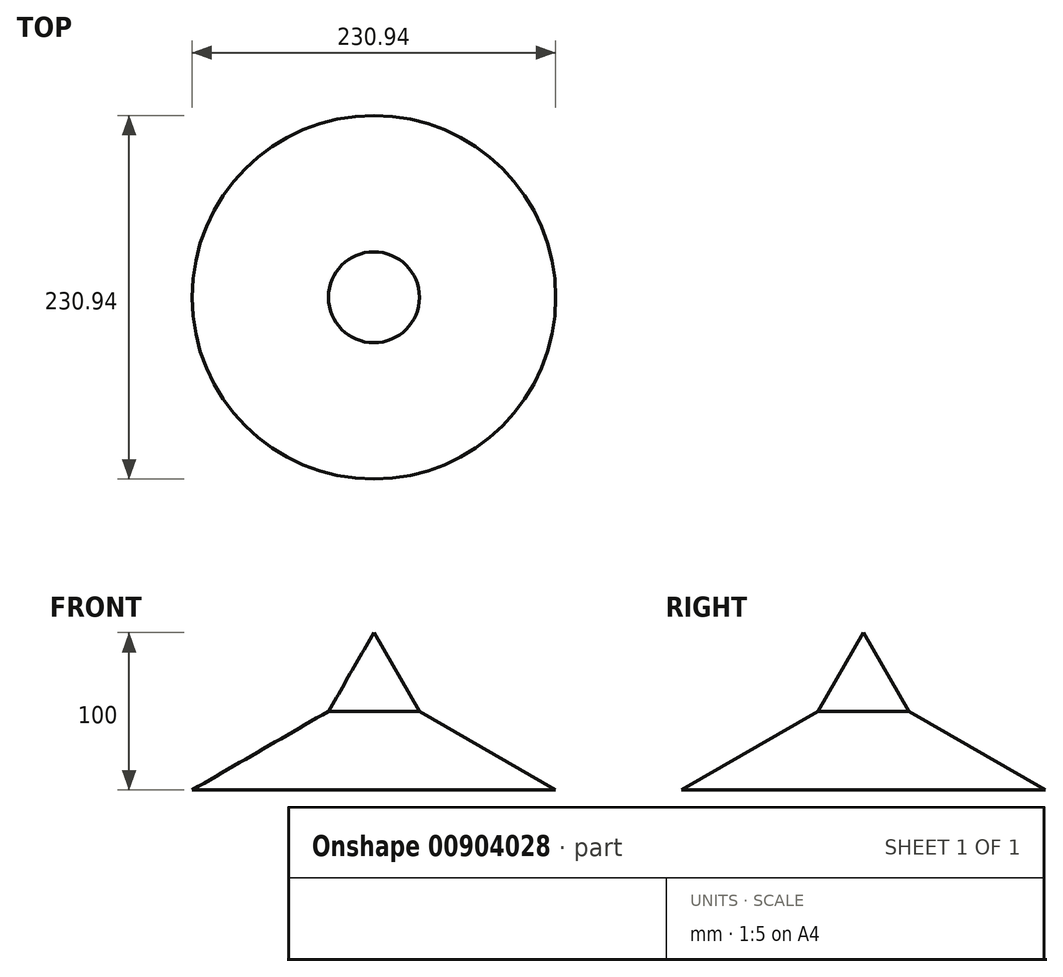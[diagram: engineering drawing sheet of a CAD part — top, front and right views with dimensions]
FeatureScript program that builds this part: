
annotation { "Feature Type Name" : "Feature", "Feature Type Description" : "" }
export const myFeature = defineFeature(function(context is Context, id is Id, definition is map)
    precondition{}
    {
        {
            var Q0;
            Q0=qCreatedBy(makeId("Front.planeOp"),FACE);
            var sketch = newSketch(context, id + "F0", { "sketchPlane" : qUnion([Q0])});
            skLineSegment(sketch, "E0", {"start": v(0, 0) * mm, "end": v(0, 100) * mm});
            skLineSegment(sketch, "E1", {"start": v(0, 100) * mm, "end": v(28.87, 50) * mm});
            skLineSegment(sketch, "E2", {"start": v(28.87, 50) * mm, "end": v(115.47, 0) * mm});
            skLineSegment(sketch, "E3", {"start": v(115.47, 0) * mm, "end": v(0, 0) * mm});
            skSolve(sketch);
        }
        {
            var Q0;
            Q0=makeQuery(id+"F0.imprint","IMPRINT",FACE,{"disambiguationData":[TD([[makeQuery(id+"F0.imprint","IMPRINT",EDGE,{"derivedFrom":sQuery(id+"F0.wireOp",EDGE,"E0")}),-1.0]])]});
            var Q1;
            Q1=sQuery(id+"F0.wireOp",EDGE,"E0");
            revolve(context, id + "F1", {"surfaceOperationType" : NewSurfaceOperationType.NEW, "entities" : qUnion([Q0]), "axis" : qUnion([Q1]), "revolveType" : RevolveType.FULL});
        }
        {
            var Q0;
            Q0=qCreatedBy(makeId("Right.planeOp"),FACE);
            cPlane(context, id + "F2", {"entities" : qUnion([Q0]), "cplaneType" : CPlaneType.OFFSET, "offset" : 10 * mm, "width" : 150 * mm, "height" : 150 * mm});
        }
    });
